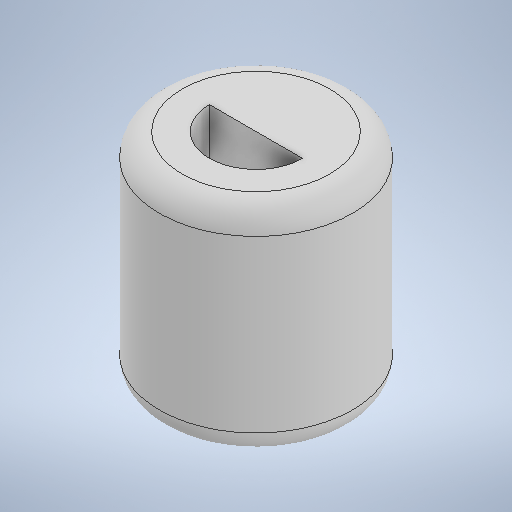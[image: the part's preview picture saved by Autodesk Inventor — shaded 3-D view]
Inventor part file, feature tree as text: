
AUTODESK INVENTOR PART (.ipt)
format: ipt  version: 2025 (Build 290162000, 162)  size: 257,536 bytes
history: native  units: mm
features: extrude x3, sketch x3, fillet x1
ambient origin geometry x8: Origin, YZ Plane, XZ Plane, XY Plane, X Axis, Y Axis, Z Axis, Center Point
bodies: Volumenkörper1 (feature_tree)
feature tree (7):
  extrude  "Extrusion1"  Depth=19.0mm TaperAngle=0.0deg
  fillet  "Rundung1"  Radius=2.0mm
  extrude  "Extrusion2"  Depth=8.2mm TaperAngle=0.0deg
  extrude  "Extrusion3"  Depth=8.2mm TaperAngle=0.0deg
  sketch  "Skizze1"  dims[d0=17.0mm d1=19.0mm d2=0.0mm d3=2.0mm]
  sketch  "Skizze2"  dims[d4=8.2mm d5=8.2mm d6=0.0mm]
  sketch  "Skizze3"  dims[d8=5.2mm d10=8.2mm d11=0.0mm]
